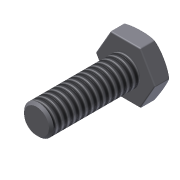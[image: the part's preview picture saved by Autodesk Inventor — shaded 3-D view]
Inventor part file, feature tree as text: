
AUTODESK INVENTOR PART (.ipt)
format: ipt  version: 2011 SP1 (Build 150282100, 282)  size: 179,200 bytes
history: native  units: in
note: dims shown in document units (in); Inventor stores cm internally (conversion verified against a paired STEP export)
features: sketch x3, extrude x2, projected_geometry x2, thread x1, chamfer x1, revolve x1, fillet x1
ambient origin geometry x8: Origin, YZ Plane, XZ Plane, XY Plane, X Axis, Y Axis, Z Axis, Center Point
bodies: Solid1 (feature_tree)
feature tree (11):
  extrude  "Extrusion1"  Depth=0.75in TaperAngle=0.0deg
  extrude  "Extrusion2"  Depth=0.1562in TaperAngle=0.0deg
  thread  "Thread1"  [1 undecoded]
  chamfer  "Chamfer1"  Distance=0.02in Angle=45.0deg
  revolve  "Revolution1"  [1 undecoded]
  fillet  "Fillet1"  [1 undecoded]
  sketch  "Sketch1"  dims[d0=0.25in d1=0.75in d2=0.0in]
  sketch  "Sketch2"  dims[d3=0.4375in d4=0.1562in d5=0.0in d6=0.75in d7=0.0in d8=0.02in d9=0.125in d10=45.0deg]
  sketch  "Sketch3"  dims[d11=90.0deg d12=0.01in]
  projected_geometry  "Projected Loop1"
  projected_geometry  "Projected Loop2"
note: 3 required parameter values undecoded (feature->parameter linkage not recoverable at this tier; creation-order binding heuristic only, values carry confidence <= 0.55)